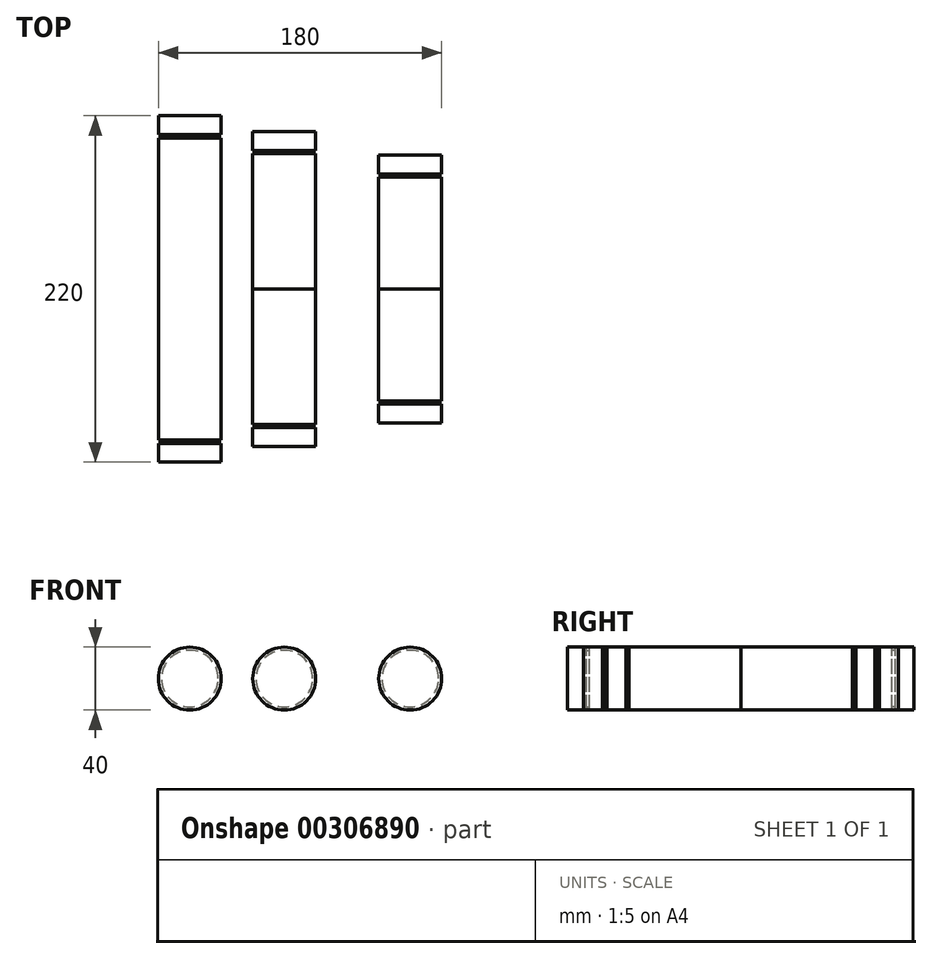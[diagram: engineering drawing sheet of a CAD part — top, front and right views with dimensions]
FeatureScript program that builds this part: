
annotation { "Feature Type Name" : "Feature", "Feature Type Description" : "" }
export const myFeature = defineFeature(function(context is Context, id is Id, definition is map)
    precondition{}
    {
        {
            assignVariable(context, id + "F0", {"name" : "pivot_circlip_offset", "anyValue" : 190});
        }
        {
            assignVariable(context, id + "F1", {"name" : "ram_base_offset", "anyValue" : 170});
        }
        {
            assignVariable(context, id + "F2", {"name" : "ram_rod_offset", "anyValue" : 140});
        }
        {
            var Q0;
            Q0=qCreatedBy(makeId("Front.planeOp"),FACE);
            var sketch = newSketch(context, id + "F3", { "sketchPlane" : qUnion([Q0])});
            skPoint(sketch, "E0", {"position": v(-100, 0) * mm});
            skCircle(sketch, "E1", {"center": v(-100, 0) * mm, "radius": 20 * mm});
            skSolve(sketch);
        }
        {
            var Q0;
            Q0 = qSketchRegion(id + "F3", true);
            extrude(context, id + "F4", {"entities" : qUnion([Q0]), "depth" : 110 * mm});
        }
        {
            var Q0;
            Q0=qCreatedBy(makeId("Front.planeOp"),FACE);
            cPlane(context, id + "F5", {"entities" : qUnion([Q0]), "cplaneType" : CPlaneType.OFFSET, "offset" : ((getVariable(context, 'pivot_circlip_offset') / 2) + 1) * mm, "width" : 150 * mm, "height" : 150 * mm});
        }
        {
            var Q0;
            Q0=qCreatedBy(id+"F5.planeOp",FACE);
            var sketch = newSketch(context, id + "F6", { "sketchPlane" : qUnion([Q0])});
            skCircle(sketch, "E2.0.0", {"center": v(-100, 0) * mm, "radius": 20 * mm, "construction": true});
            skCircle(sketch, "E3", {"center": v(-100, 0) * mm, "radius": 20 * mm});
            skCircle(sketch, "E4", {"center": v(-100, 0) * mm, "radius": 18 * mm});
            skSolve(sketch);
        }
        {
            var Q0;
            Q0 = qSketchRegion(id + "F6", true);
            extrude(context, id + "F7", {"entities" : qUnion([Q0]), "operationType" : NewBodyOperationType.REMOVE, "depth" : 2 * mm});
        }
        {
            var Q0;
            Q0=makeQuery(id+"F4.opExtrude","SWEPT_BODY",BODY,{"disambiguationData":[OSD([sQuery(id+"F3.wireOp",EDGE,"E1")])]});
            var Q1;
            Q1=qCreatedBy(makeId("Front.planeOp"),FACE);
            mirror(context, id + "F8", {"operationType" : NewBodyOperationType.ADD, "entities" : qUnion([Q0]), "mirrorPlane" : qUnion([Q1])});
        }
        {
            var Q0;
            Q0=qCreatedBy(makeId("Front.planeOp"),FACE);
            var sketch = newSketch(context, id + "F9", { "sketchPlane" : qUnion([Q0])});
            skPoint(sketch, "E5", {"position": v(-40, 0) * mm});
            skCircle(sketch, "E6", {"center": v(-40, 0) * mm, "radius": 20 * mm});
            skSolve(sketch);
        }
        {
            var Q0;
            Q0 = qSketchRegion(id + "F9", true);
            extrude(context, id + "F10", {"entities" : qUnion([Q0]), "depth" : ((getVariable(context, 'ram_base_offset') / 2) + 15) * mm});
        }
        {
            var Q0;
            Q0=qCreatedBy(makeId("Front.planeOp"),FACE);
            cPlane(context, id + "F11", {"entities" : qUnion([Q0]), "cplaneType" : CPlaneType.OFFSET, "offset" : ((getVariable(context, 'ram_base_offset') / 2) + 1) * mm, "width" : 150 * mm, "height" : 150 * mm});
        }
        {
            var Q0;
            Q0=qCreatedBy(id+"F11.planeOp",FACE);
            var sketch = newSketch(context, id + "F12", { "sketchPlane" : qUnion([Q0])});
            skCircle(sketch, "E7.0", {"center": v(-40, 0) * mm, "radius": 20 * mm});
            skCircle(sketch, "E8", {"center": v(-40, 0) * mm, "radius": 18 * mm});
            skSolve(sketch);
        }
        {
            var Q0;
            Q0 = qSketchRegion(id + "F12", true);
            extrude(context, id + "F13", {"entities" : qUnion([Q0]), "operationType" : NewBodyOperationType.REMOVE, "depth" : 2 * mm});
        }
        {
            var Q0;
            Q0=makeQuery(id+"F10.opExtrude","SWEPT_BODY",BODY,{"disambiguationData":[OSD([sQuery(id+"F9.wireOp",EDGE,"E6")])]});
            var Q1;
            Q1=qCreatedBy(makeId("Front.planeOp"),FACE);
            mirror(context, id + "F14", {"operationType" : NewBodyOperationType.ADD, "entities" : qUnion([Q0]), "mirrorPlane" : qUnion([Q1])});
        }
        {
            var Q0;
            Q0=qCreatedBy(makeId("Front.planeOp"),FACE);
            var sketch = newSketch(context, id + "F15", { "sketchPlane" : qUnion([Q0])});
            skPoint(sketch, "E9", {"position": v(40, 0) * mm});
            skCircle(sketch, "E10", {"center": v(40, 0) * mm, "radius": 20 * mm});
            skSolve(sketch);
        }
        {
            var Q0;
            Q0 = qSketchRegion(id + "F15", true);
            extrude(context, id + "F16", {"entities" : qUnion([Q0]), "depth" : (getVariable(context, 'ram_rod_offset') / 2 + 15) * mm});
        }
        {
            var Q0;
            Q0=qCreatedBy(makeId("Front.planeOp"),FACE);
            cPlane(context, id + "F17", {"entities" : qUnion([Q0]), "cplaneType" : CPlaneType.OFFSET, "offset" : ((getVariable(context, 'ram_rod_offset') / 2) + 1) * mm, "width" : 150 * mm, "height" : 150 * mm});
        }
        {
            var Q0;
            Q0=qCreatedBy(id+"F17.planeOp",FACE);
            var sketch = newSketch(context, id + "F18", { "sketchPlane" : qUnion([Q0])});
            skCircle(sketch, "E11.0", {"center": v(40, 0) * mm, "radius": 20 * mm});
            skCircle(sketch, "E12", {"center": v(40, 0) * mm, "radius": 18 * mm});
            skSolve(sketch);
        }
        {
            var Q0;
            Q0 = qSketchRegion(id + "F18", true);
            extrude(context, id + "F19", {"entities" : qUnion([Q0]), "operationType" : NewBodyOperationType.REMOVE, "depth" : 2 * mm});
        }
        {
            var Q0;
            Q0=makeQuery(id+"F16.opExtrude","SWEPT_BODY",BODY,{"disambiguationData":[OSD([sQuery(id+"F15.wireOp",EDGE,"E10")])]});
            var Q1;
            Q1=qCreatedBy(makeId("Front.planeOp"),FACE);
            mirror(context, id + "F20", {"operationType" : NewBodyOperationType.ADD, "entities" : qUnion([Q0]), "mirrorPlane" : qUnion([Q1])});
        }
    });
